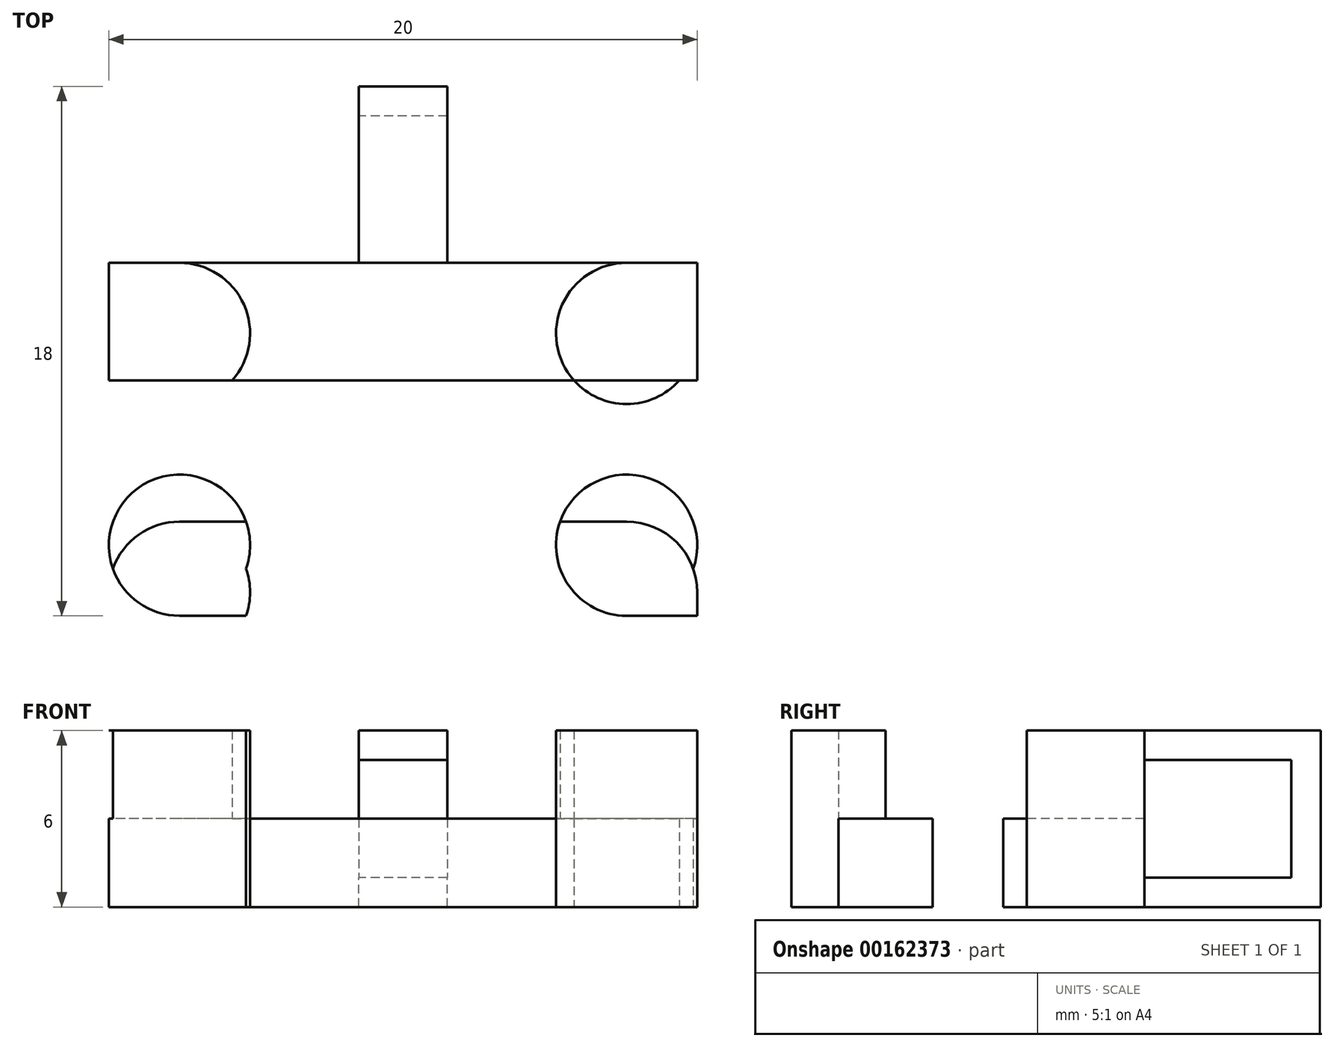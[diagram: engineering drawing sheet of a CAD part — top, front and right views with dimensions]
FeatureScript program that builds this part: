
annotation { "Feature Type Name" : "Feature", "Feature Type Description" : "" }
export const myFeature = defineFeature(function(context is Context, id is Id, definition is map)
    precondition{}
    {
        {
            var Q0;
            Q0=qCreatedBy(makeId("Top.planeOp"),FACE);
            var sketch = newSketch(context, id + "F0", { "sketchPlane" : qUnion([Q0])});
            skLineSegment(sketch, "E0.bottom", {"start": v(10, 6) * mm, "end": v(-10, 6) * mm});
            skLineSegment(sketch, "E0.top", {"start": v(10, -6) * mm, "end": v(-10, -6) * mm});
            skLineSegment(sketch, "E0.left", {"start": v(10, 6) * mm, "end": v(10, -6) * mm});
            skLineSegment(sketch, "E0.right", {"start": v(-10, 6) * mm, "end": v(-10, -6) * mm});
            skPoint(sketch, "E0.middle", {"position": v(0, 0) * mm});
            skLineSegment(sketch, "E1.bottom", {"start": v(-7.6, 3.6) * mm, "end": v(7.6, 3.6) * mm, "construction": true});
            skLineSegment(sketch, "E1.top", {"start": v(-7.6, -3.6) * mm, "end": v(7.6, -3.6) * mm, "construction": true});
            skLineSegment(sketch, "E1.left", {"start": v(-7.6, 3.6) * mm, "end": v(-7.6, -3.6) * mm, "construction": true});
            skLineSegment(sketch, "E1.right", {"start": v(7.6, 3.6) * mm, "end": v(7.6, -3.6) * mm, "construction": true});
            skCircle(sketch, "E2", {"center": v(-7.6, 3.6) * mm, "radius": 2.4 * mm});
            skCircle(sketch, "E3", {"center": v(-7.6, -3.6) * mm, "radius": 2.4 * mm});
            skCircle(sketch, "E4", {"center": v(7.6, -3.6) * mm, "radius": 2.4 * mm});
            skCircle(sketch, "E5", {"center": v(7.6, 3.6) * mm, "radius": 2.4 * mm});
            skLineSegment(sketch, "E6.bottom", {"start": v(-10, -2.8) * mm, "end": v(10, -2.8) * mm, "construction": true});
            skLineSegment(sketch, "E6.top", {"start": v(-10, -7.6) * mm, "end": v(10, -7.6) * mm, "construction": true});
            skLineSegment(sketch, "E6.left", {"start": v(-10, -2.8) * mm, "end": v(-10, -7.6) * mm, "construction": true});
            skLineSegment(sketch, "E6.right", {"start": v(10, -2.8) * mm, "end": v(10, -7.6) * mm, "construction": true});
            skCircle(sketch, "E7", {"center": v(-7.6, -5.2) * mm, "radius": 2.4 * mm});
            skPoint(sketch, "E7.first.point", {"position": v(-10, -5.2) * mm});
            skPoint(sketch, "E7.second.point", {"position": v(-7.6, -2.8) * mm});
            skPoint(sketch, "E7.third.point", {"position": v(-7.6, -7.6) * mm});
            skCircle(sketch, "E8", {"center": v(7.6, -5.2) * mm, "radius": 2.4 * mm});
            skPoint(sketch, "E8.first.point", {"position": v(10, -5.2) * mm});
            skPoint(sketch, "E8.second.point", {"position": v(7.6, -7.6) * mm});
            skPoint(sketch, "E8.third.point", {"position": v(7.6, -2.8) * mm});
            skLineSegment(sketch, "E9", {"start": v(-7.6, -2.8) * mm, "end": v(7.6, -2.8) * mm});
            skLineSegment(sketch, "E10.bottom", {"start": v(-10, 6) * mm, "end": v(10, 6) * mm});
            skLineSegment(sketch, "E10.top", {"start": v(-10, 2) * mm, "end": v(10, 2) * mm});
            skLineSegment(sketch, "E10.left", {"start": v(-10, 6) * mm, "end": v(-10, 2) * mm});
            skLineSegment(sketch, "E10.right", {"start": v(10, 6) * mm, "end": v(10, 2) * mm});
            skPoint(sketch, "E10.middle", {"position": v(0, 4) * mm});
            skPoint(sketch, "E10.middle.positionSnap0", {"position": v(0, 6) * mm});
            skPoint(sketch, "E10.centerSnap0", {"position": v(0, 6) * mm});
            skSolve(sketch);
        }
        {
            var Q0;
            {var subQ5=sQuery(id+"F0.wireOp",EDGE,"E5");var subQ17=sQuery(id+"F0.wireOp",EDGE,"E0.bottom");var subQ18=makeQuery(id+"F0.imprint","INTERSECT",VERTEX,{"derivedFrom":[subQ17,subQ5]});Q0=makeQuery(id+"F0.imprint","IMPRINT",FACE,{"disambiguationData":[TD([[makeQuery(id+"F0.imprint","IMPRINT",EDGE,{"disambiguationData":[TD([[subQ18,-1.0]])],"derivedFrom":subQ17}),1.0]])]});}
            var Q1;
            {var subQ0=sQuery(id+"F0.wireOp",EDGE,"E4");var subQ1=makeQuery(id+"F0.imprint","INTERSECT",VERTEX,{"derivedFrom":[sQuery(id+"F0.wireOp",EDGE,"E0.top"),subQ0]});Q1=makeQuery(id+"F0.imprint","IMPRINT",FACE,{"disambiguationData":[TD([[makeQuery(id+"F0.imprint","IMPRINT",EDGE,{"disambiguationData":[TD([[subQ1,1.0]])],"derivedFrom":subQ0}),1.0]])]});}
            var Q2;
            {var subQ0=sQuery(id+"F0.wireOp",EDGE,"E4");var subQ1=makeQuery(id+"F0.imprint","INTERSECT",VERTEX,{"derivedFrom":[sQuery(id+"F0.wireOp",EDGE,"E0.left"),subQ0]});Q2=makeQuery(id+"F0.imprint","IMPRINT",FACE,{"disambiguationData":[TD([[makeQuery(id+"F0.imprint","IMPRINT",EDGE,{"disambiguationData":[TD([[subQ1,-1.0]])],"derivedFrom":subQ0}),1.0]])]});}
            var Q3;
            {var subQ0=sQuery(id+"F0.wireOp",EDGE,"E8");var subQ1=sQuery(id+"F0.wireOp",EDGE,"E0.top");var subQ2=makeQuery(id+"F0.imprint","INTERSECT",VERTEX,{"disambiguationData":[OD(1.0)],"derivedFrom":[subQ1,subQ0]});Q3=makeQuery(id+"F0.imprint","IMPRINT",FACE,{"disambiguationData":[TD([[makeQuery(id+"F0.imprint","IMPRINT",EDGE,{"disambiguationData":[TD([[subQ2,1.0]])],"derivedFrom":subQ1}),-1.0]])]});}
            var Q4;
            {var subQ0=sQuery(id+"F0.wireOp",EDGE,"E7");var subQ1=sQuery(id+"F0.wireOp",EDGE,"E0.top");var subQ2=makeQuery(id+"F0.imprint","INTERSECT",VERTEX,{"disambiguationData":[OD(0.0)],"derivedFrom":[subQ1,subQ0]});Q4=makeQuery(id+"F0.imprint","IMPRINT",FACE,{"disambiguationData":[TD([[makeQuery(id+"F0.imprint","IMPRINT",EDGE,{"disambiguationData":[TD([[subQ2,-1.0]])],"derivedFrom":subQ1}),-1.0]])]});}
            var Q5;
            {var subQ0=sQuery(id+"F0.wireOp",EDGE,"E3");var subQ1=makeQuery(id+"F0.imprint","INTERSECT",VERTEX,{"derivedFrom":[sQuery(id+"F0.wireOp",EDGE,"E0.top"),subQ0]});Q5=makeQuery(id+"F0.imprint","IMPRINT",FACE,{"disambiguationData":[TD([[makeQuery(id+"F0.imprint","IMPRINT",EDGE,{"disambiguationData":[TD([[subQ1,1.0]])],"derivedFrom":subQ0}),1.0]])]});}
            var Q6;
            {var subQ0=sQuery(id+"F0.wireOp",EDGE,"E3");var subQ1=makeQuery(id+"F0.imprint","INTERSECT",VERTEX,{"derivedFrom":[sQuery(id+"F0.wireOp",EDGE,"E0.right"),subQ0]});Q6=makeQuery(id+"F0.imprint","IMPRINT",FACE,{"disambiguationData":[TD([[makeQuery(id+"F0.imprint","IMPRINT",EDGE,{"disambiguationData":[TD([[subQ1,-1.0]])],"derivedFrom":subQ0}),1.0]])]});}
            var Q7;
            {var subQ0=sQuery(id+"F0.wireOp",EDGE,"E2");var subQ1=makeQuery(id+"F0.imprint","INTERSECT",VERTEX,{"derivedFrom":[sQuery(id+"F0.wireOp",EDGE,"E0.bottom"),subQ0]});Q7=makeQuery(id+"F0.imprint","IMPRINT",FACE,{"disambiguationData":[TD([[makeQuery(id+"F0.imprint","IMPRINT",EDGE,{"disambiguationData":[TD([[subQ1,-1.0]])],"derivedFrom":subQ0}),1.0]])]});}
            var Q8;
            {var subQ0=sQuery(id+"F0.wireOp",EDGE,"E5");var subQ1=makeQuery(id+"F0.imprint","INTERSECT",VERTEX,{"derivedFrom":[sQuery(id+"F0.wireOp",EDGE,"E0.bottom"),subQ0]});Q8=makeQuery(id+"F0.imprint","IMPRINT",FACE,{"disambiguationData":[TD([[makeQuery(id+"F0.imprint","IMPRINT",EDGE,{"disambiguationData":[TD([[subQ1,1.0]])],"derivedFrom":subQ0}),1.0]])]});}
            var Q9;
            {var subQ3=sQuery(id+"F0.wireOp",EDGE,"E8");var subQ9=sQuery(id+"F0.wireOp",EDGE,"E0.top");var subQ11=makeQuery(id+"F0.imprint","INTERSECT",VERTEX,{"disambiguationData":[OD(1.0)],"derivedFrom":[subQ9,subQ3]});Q9=makeQuery(id+"F0.imprint","IMPRINT",FACE,{"disambiguationData":[TD([[makeQuery(id+"F0.imprint","IMPRINT",EDGE,{"disambiguationData":[TD([[subQ11,-1.0]])],"derivedFrom":subQ9}),-1.0]])]});}
            var Q10;
            {var subQ0=sQuery(id+"F0.wireOp",EDGE,"E9");var subQ1=sQuery(id+"F0.wireOp",EDGE,"E3");var subQ2=makeQuery(id+"F0.imprint","INTERSECT",VERTEX,{"derivedFrom":[subQ1,subQ0]});Q10=makeQuery(id+"F0.imprint","IMPRINT",FACE,{"disambiguationData":[TD([[makeQuery(id+"F0.imprint","IMPRINT",EDGE,{"disambiguationData":[TD([[subQ2,1.0]])],"derivedFrom":subQ1}),1.0]])]});}
            var Q11;
            {var subQ0=sQuery(id+"F0.wireOp",EDGE,"E9");var subQ1=sQuery(id+"F0.wireOp",EDGE,"E4");var subQ2=makeQuery(id+"F0.imprint","INTERSECT",VERTEX,{"derivedFrom":[subQ1,subQ0]});Q11=makeQuery(id+"F0.imprint","IMPRINT",FACE,{"disambiguationData":[TD([[makeQuery(id+"F0.imprint","IMPRINT",EDGE,{"disambiguationData":[TD([[subQ2,-1.0]])],"derivedFrom":subQ1}),1.0]])]});}
            var Q12;
            {var subQ0=sQuery(id+"F0.wireOp",EDGE,"E10.bottom");var subQ1=sQuery(id+"F0.wireOp",EDGE,"E2");var subQ2=makeQuery(id+"F0.imprint","INTERSECT",VERTEX,{"derivedFrom":[subQ1,subQ0]});Q12=makeQuery(id+"F0.imprint","IMPRINT",FACE,{"disambiguationData":[TD([[makeQuery(id+"F0.imprint","IMPRINT",EDGE,{"disambiguationData":[TD([[subQ2,1.0]])],"derivedFrom":subQ1}),-1.0]])]});}
            var Q13;
            {var subQ7=sQuery(id+"F0.wireOp",EDGE,"E10.top");var subQ8=sQuery(id+"F0.wireOp",EDGE,"E2");var subQ9=makeQuery(id+"F0.imprint","INTERSECT",VERTEX,{"disambiguationData":[OD(0.0)],"derivedFrom":[subQ8,subQ7]});Q13=makeQuery(id+"F0.imprint","IMPRINT",FACE,{"disambiguationData":[TD([[makeQuery(id+"F0.imprint","IMPRINT",EDGE,{"disambiguationData":[TD([[subQ9,-1.0]])],"derivedFrom":subQ8}),-1.0]])]});}
            var Q14;
            {var subQ0=sQuery(id+"F0.wireOp",EDGE,"E10.top");var subQ1=sQuery(id+"F0.wireOp",EDGE,"E5");var subQ2=makeQuery(id+"F0.imprint","INTERSECT",VERTEX,{"disambiguationData":[OD(0.0)],"derivedFrom":[subQ1,subQ0]});Q14=makeQuery(id+"F0.imprint","IMPRINT",FACE,{"disambiguationData":[TD([[makeQuery(id+"F0.imprint","IMPRINT",EDGE,{"disambiguationData":[TD([[subQ2,-1.0]])],"derivedFrom":subQ1}),1.0]])]});}
            var Q15;
            {var subQ0=sQuery(id+"F0.wireOp",EDGE,"E10.top");var subQ1=sQuery(id+"F0.wireOp",EDGE,"E2");var subQ2=makeQuery(id+"F0.imprint","INTERSECT",VERTEX,{"disambiguationData":[OD(0.0)],"derivedFrom":[subQ1,subQ0]});Q15=makeQuery(id+"F0.imprint","IMPRINT",FACE,{"disambiguationData":[TD([[makeQuery(id+"F0.imprint","IMPRINT",EDGE,{"disambiguationData":[TD([[subQ2,-1.0]])],"derivedFrom":subQ1}),1.0]])]});}
            var Q16;
            {var subQ0=sQuery(id+"F0.wireOp",EDGE,"E10.left");var subQ1=sQuery(id+"F0.wireOp",EDGE,"E2");var subQ2=makeQuery(id+"F0.imprint","INTERSECT",VERTEX,{"derivedFrom":[subQ1,subQ0]});Q16=makeQuery(id+"F0.imprint","IMPRINT",FACE,{"disambiguationData":[TD([[makeQuery(id+"F0.imprint","IMPRINT",EDGE,{"disambiguationData":[TD([[subQ2,-1.0]])],"derivedFrom":subQ1}),-1.0]])]});}
            var Q17;
            {var subQ0=sQuery(id+"F0.wireOp",EDGE,"E10.right");var subQ1=sQuery(id+"F0.wireOp",EDGE,"E5");var subQ2=makeQuery(id+"F0.imprint","INTERSECT",VERTEX,{"derivedFrom":[subQ1,subQ0]});Q17=makeQuery(id+"F0.imprint","IMPRINT",FACE,{"disambiguationData":[TD([[makeQuery(id+"F0.imprint","IMPRINT",EDGE,{"disambiguationData":[TD([[subQ2,1.0]])],"derivedFrom":subQ1}),-1.0]])]});}
            extrude(context, id + "F1", {"entities" : qUnion([Q0, Q1, Q2, Q3, Q4, Q5, Q6, Q7, Q8, Q9, Q10, Q11, Q12, Q13, Q14, Q15, Q16, Q17]), "depth" : 3 * mm});
        }
        {
            var Q0;
            {var subQ3=sQuery(id+"F0.wireOp",EDGE,"E8");var subQ9=sQuery(id+"F0.wireOp",EDGE,"E0.top");var subQ11=makeQuery(id+"F0.imprint","INTERSECT",VERTEX,{"disambiguationData":[OD(1.0)],"derivedFrom":[subQ9,subQ3]});Q0=makeQuery(id+"F0.imprint","IMPRINT",FACE,{"disambiguationData":[TD([[makeQuery(id+"F0.imprint","IMPRINT",EDGE,{"disambiguationData":[TD([[subQ11,-1.0]])],"derivedFrom":subQ9}),-1.0]])]});}
            var Q1;
            {var subQ0=sQuery(id+"F0.wireOp",EDGE,"E3");var subQ1=makeQuery(id+"F0.imprint","INTERSECT",VERTEX,{"derivedFrom":[sQuery(id+"F0.wireOp",EDGE,"E0.top"),subQ0]});Q1=makeQuery(id+"F0.imprint","IMPRINT",FACE,{"disambiguationData":[TD([[makeQuery(id+"F0.imprint","IMPRINT",EDGE,{"disambiguationData":[TD([[subQ1,1.0]])],"derivedFrom":subQ0}),1.0]])]});}
            var Q2;
            {var subQ0=sQuery(id+"F0.wireOp",EDGE,"E7");var subQ1=sQuery(id+"F0.wireOp",EDGE,"E0.top");var subQ2=makeQuery(id+"F0.imprint","INTERSECT",VERTEX,{"disambiguationData":[OD(0.0)],"derivedFrom":[subQ1,subQ0]});Q2=makeQuery(id+"F0.imprint","IMPRINT",FACE,{"disambiguationData":[TD([[makeQuery(id+"F0.imprint","IMPRINT",EDGE,{"disambiguationData":[TD([[subQ2,-1.0]])],"derivedFrom":subQ1}),-1.0]])]});}
            var Q3;
            {var subQ0=sQuery(id+"F0.wireOp",EDGE,"E9");var subQ1=sQuery(id+"F0.wireOp",EDGE,"E3");var subQ2=makeQuery(id+"F0.imprint","INTERSECT",VERTEX,{"derivedFrom":[subQ1,subQ0]});Q3=makeQuery(id+"F0.imprint","IMPRINT",FACE,{"disambiguationData":[TD([[makeQuery(id+"F0.imprint","IMPRINT",EDGE,{"disambiguationData":[TD([[subQ2,1.0]])],"derivedFrom":subQ1}),1.0]])]});}
            var Q4;
            {var subQ0=sQuery(id+"F0.wireOp",EDGE,"E4");var subQ1=makeQuery(id+"F0.imprint","INTERSECT",VERTEX,{"derivedFrom":[sQuery(id+"F0.wireOp",EDGE,"E0.top"),subQ0]});Q4=makeQuery(id+"F0.imprint","IMPRINT",FACE,{"disambiguationData":[TD([[makeQuery(id+"F0.imprint","IMPRINT",EDGE,{"disambiguationData":[TD([[subQ1,1.0]])],"derivedFrom":subQ0}),1.0]])]});}
            var Q5;
            {var subQ0=sQuery(id+"F0.wireOp",EDGE,"E8");var subQ1=sQuery(id+"F0.wireOp",EDGE,"E0.top");var subQ2=makeQuery(id+"F0.imprint","INTERSECT",VERTEX,{"disambiguationData":[OD(1.0)],"derivedFrom":[subQ1,subQ0]});Q5=makeQuery(id+"F0.imprint","IMPRINT",FACE,{"disambiguationData":[TD([[makeQuery(id+"F0.imprint","IMPRINT",EDGE,{"disambiguationData":[TD([[subQ2,1.0]])],"derivedFrom":subQ1}),-1.0]])]});}
            var Q6;
            {var subQ0=sQuery(id+"F0.wireOp",EDGE,"E9");var subQ1=sQuery(id+"F0.wireOp",EDGE,"E4");var subQ2=makeQuery(id+"F0.imprint","INTERSECT",VERTEX,{"derivedFrom":[subQ1,subQ0]});Q6=makeQuery(id+"F0.imprint","IMPRINT",FACE,{"disambiguationData":[TD([[makeQuery(id+"F0.imprint","IMPRINT",EDGE,{"disambiguationData":[TD([[subQ2,-1.0]])],"derivedFrom":subQ1}),1.0]])]});}
            var Q7;
            {var subQ0=sQuery(id+"F0.wireOp",EDGE,"E2");var subQ1=makeQuery(id+"F0.imprint","INTERSECT",VERTEX,{"derivedFrom":[subQ0,sQuery(id+"F0.wireOp",EDGE,"E10.left")]});Q7=makeQuery(id+"F0.imprint","IMPRINT",FACE,{"disambiguationData":[TD([[makeQuery(id+"F0.imprint","IMPRINT",EDGE,{"disambiguationData":[TD([[subQ1,1.0]])],"derivedFrom":subQ0}),1.0]])]});}
            var Q8;
            {var subQ0=sQuery(id+"F0.wireOp",EDGE,"E10.bottom");var subQ1=sQuery(id+"F0.wireOp",EDGE,"E2");var subQ2=makeQuery(id+"F0.imprint","INTERSECT",VERTEX,{"derivedFrom":[subQ1,subQ0]});Q8=makeQuery(id+"F0.imprint","IMPRINT",FACE,{"disambiguationData":[TD([[makeQuery(id+"F0.imprint","IMPRINT",EDGE,{"disambiguationData":[TD([[subQ2,1.0]])],"derivedFrom":subQ1}),-1.0]])]});}
            var Q9;
            {var subQ0=sQuery(id+"F0.wireOp",EDGE,"E5");var subQ1=makeQuery(id+"F0.imprint","INTERSECT",VERTEX,{"derivedFrom":[subQ0,sQuery(id+"F0.wireOp",EDGE,"E10.bottom")]});Q9=makeQuery(id+"F0.imprint","IMPRINT",FACE,{"disambiguationData":[TD([[makeQuery(id+"F0.imprint","IMPRINT",EDGE,{"disambiguationData":[TD([[subQ1,1.0]])],"derivedFrom":subQ0}),1.0]])]});}
            var Q10;
            {var subQ0=sQuery(id+"F0.wireOp",EDGE,"E10.right");var subQ1=sQuery(id+"F0.wireOp",EDGE,"E5");var subQ2=makeQuery(id+"F0.imprint","INTERSECT",VERTEX,{"derivedFrom":[subQ1,subQ0]});Q10=makeQuery(id+"F0.imprint","IMPRINT",FACE,{"disambiguationData":[TD([[makeQuery(id+"F0.imprint","IMPRINT",EDGE,{"disambiguationData":[TD([[subQ2,1.0]])],"derivedFrom":subQ1}),-1.0]])]});}
            var Q11;
            {var subQ0=sQuery(id+"F0.wireOp",EDGE,"E10.left");var subQ1=sQuery(id+"F0.wireOp",EDGE,"E2");var subQ2=makeQuery(id+"F0.imprint","INTERSECT",VERTEX,{"derivedFrom":[subQ1,subQ0]});Q11=makeQuery(id+"F0.imprint","IMPRINT",FACE,{"disambiguationData":[TD([[makeQuery(id+"F0.imprint","IMPRINT",EDGE,{"disambiguationData":[TD([[subQ2,-1.0]])],"derivedFrom":subQ1}),-1.0]])]});}
            extrude(context, id + "F2", {"entities" : qUnion([Q0, Q1, Q2, Q3, Q4, Q5, Q6, Q7, Q8, Q9, Q10, Q11]), "operationType" : NewBodyOperationType.ADD, "depth" : 6 * mm});
        }
        {
            var Q0;
            Q0=qCreatedBy(makeId("Right.planeOp"),FACE);
            var sketch = newSketch(context, id + "F3", { "sketchPlane" : qUnion([Q0])});
            skLineSegment(sketch, "E11.bottom", {"start": v(6, 0) * mm, "end": v(12, 0) * mm});
            skLineSegment(sketch, "E11.top", {"start": v(6, 6) * mm, "end": v(12, 6) * mm});
            skLineSegment(sketch, "E11.left", {"start": v(6, 0) * mm, "end": v(6, 6) * mm});
            skLineSegment(sketch, "E11.right", {"start": v(12, 0) * mm, "end": v(12, 6) * mm});
            skLineSegment(sketch, "E12.bottom", {"start": v(6, 5) * mm, "end": v(11, 5) * mm});
            skLineSegment(sketch, "E12.top", {"start": v(6, 1) * mm, "end": v(11, 1) * mm});
            skLineSegment(sketch, "E12.left", {"start": v(6, 5) * mm, "end": v(6, 1) * mm});
            skLineSegment(sketch, "E12.right", {"start": v(11, 5) * mm, "end": v(11, 1) * mm});
            skSolve(sketch);
        }
        {
            var Q0;
            {var subQ4=sQuery(id+"F3.wireOp",EDGE,"E11.bottom");Q0=makeQuery(id+"F3.imprint","IMPRINT",FACE,{"disambiguationData":[TD([[makeQuery(id+"F3.imprint","IMPRINT",EDGE,{"derivedFrom":subQ4}),1.0]])]});}
            extrude(context, id + "F4", {"entities" : qUnion([Q0]), "operationType" : NewBodyOperationType.ADD, "depth" : 1.5 * mm, "hasSecondDirection" : true, "secondDirectionOppositeDirection" : true, "secondDirectionDepth" : 1.5 * mm});
        }
    });
